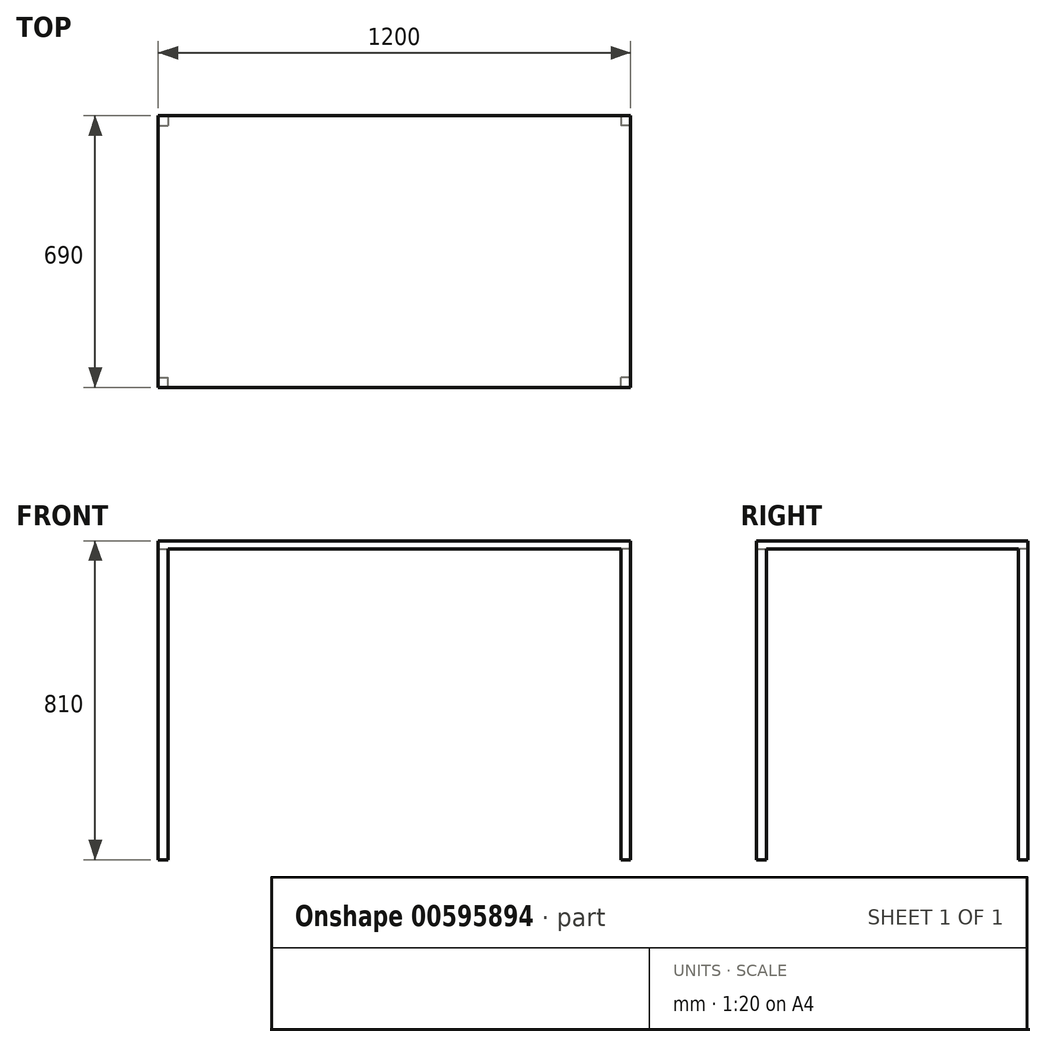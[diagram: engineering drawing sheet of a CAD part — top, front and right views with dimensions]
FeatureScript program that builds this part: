
annotation { "Feature Type Name" : "Feature", "Feature Type Description" : "" }
export const myFeature = defineFeature(function(context is Context, id is Id, definition is map)
    precondition{}
    {
        {
            var Q0;
            Q0=qCreatedBy(makeId("Top.planeOp"),FACE);
            var sketch = newSketch(context, id + "F0", { "sketchPlane" : qUnion([Q0])});
            skLineSegment(sketch, "E0.bottom", {"start": v(600, 345) * mm, "end": v(-600, 345) * mm});
            skLineSegment(sketch, "E0.top", {"start": v(600, -345) * mm, "end": v(-600, -345) * mm});
            skLineSegment(sketch, "E0.left", {"start": v(600, 345) * mm, "end": v(600, -345) * mm});
            skLineSegment(sketch, "E0.right", {"start": v(-600, 345) * mm, "end": v(-600, -345) * mm});
            skPoint(sketch, "E0.middle", {"position": v(0, 0) * mm});
            skSolve(sketch);
        }
        {
            var Q0;
            Q0=makeQuery(id+"F0.imprint","IMPRINT",FACE,{"disambiguationData":[TD([[makeQuery(id+"F0.imprint","IMPRINT",EDGE,{"derivedFrom":sQuery(id+"F0.wireOp",EDGE,"E0.bottom")}),1.0]])]});
            extrude(context, id + "F1", {"entities" : qUnion([Q0]), "oppositeDirection" : true, "depth" : 20 * mm, "offsetDistance" : 25 * mm});
        }
        {
            var Q0;
            Q0=makeQuery(id+"F1.opExtrude","CAP_FACE",FACE,{"disambiguationData":[OSD([sQuery(id+"F0.wireOp",EDGE,"E0.bottom"),sQuery(id+"F0.wireOp",EDGE,"E0.top"),sQuery(id+"F0.wireOp",EDGE,"E0.left"),sQuery(id+"F0.wireOp",EDGE,"E0.right")])],"isStart":false});
            var sketch = newSketch(context, id + "F2", { "sketchPlane" : qUnion([Q0])});
            skLineSegment(sketch, "E1.bottom", {"start": v(600, 345) * mm, "end": v(575, 345) * mm});
            skLineSegment(sketch, "E1.top", {"start": v(600, 320) * mm, "end": v(575, 320) * mm});
            skLineSegment(sketch, "E1.left", {"start": v(600, 345) * mm, "end": v(600, 320) * mm});
            skLineSegment(sketch, "E1.right", {"start": v(575, 345) * mm, "end": v(575, 320) * mm});
            skLineSegment(sketch, "E2.MirrorCS", {"start": v(-575, 345) * mm, "end": v(-575, 320) * mm});
            skLineSegment(sketch, "E3.MirrorCS", {"start": v(-600, 345) * mm, "end": v(-600, 320) * mm});
            skLineSegment(sketch, "E4.MirrorCS", {"start": v(-600, 320) * mm, "end": v(-575, 320) * mm});
            skLineSegment(sketch, "E5.MirrorCS", {"start": v(-600, 345) * mm, "end": v(-575, 345) * mm});
            skLineSegment(sketch, "E6.MirrorCS", {"start": v(575, -345) * mm, "end": v(575, -320) * mm});
            skLineSegment(sketch, "E7.MirrorCS", {"start": v(600, -345) * mm, "end": v(600, -320) * mm});
            skLineSegment(sketch, "E8.MirrorCS", {"start": v(600, -320) * mm, "end": v(575, -320) * mm});
            skLineSegment(sketch, "E9.MirrorCS", {"start": v(600, -345) * mm, "end": v(575, -345) * mm});
            skLineSegment(sketch, "E10.MirrorCS", {"start": v(-600, -320) * mm, "end": v(-575, -320) * mm});
            skLineSegment(sketch, "E11.MirrorCS", {"start": v(-600, -345) * mm, "end": v(-600, -320) * mm});
            skLineSegment(sketch, "E12.MirrorCS", {"start": v(-575, -345) * mm, "end": v(-575, -320) * mm});
            skLineSegment(sketch, "E13.MirrorCS", {"start": v(-600, -345) * mm, "end": v(-575, -345) * mm});
            skSolve(sketch);
        }
        {
            var Q0;
            Q0 = qSketchRegion(id + "F2", true);
            extrude(context, id + "F3", {"entities" : qUnion([Q0]), "operationType" : NewBodyOperationType.ADD, "depth" : 790 * mm, "offsetDistance" : 25 * mm});
        }
    });
